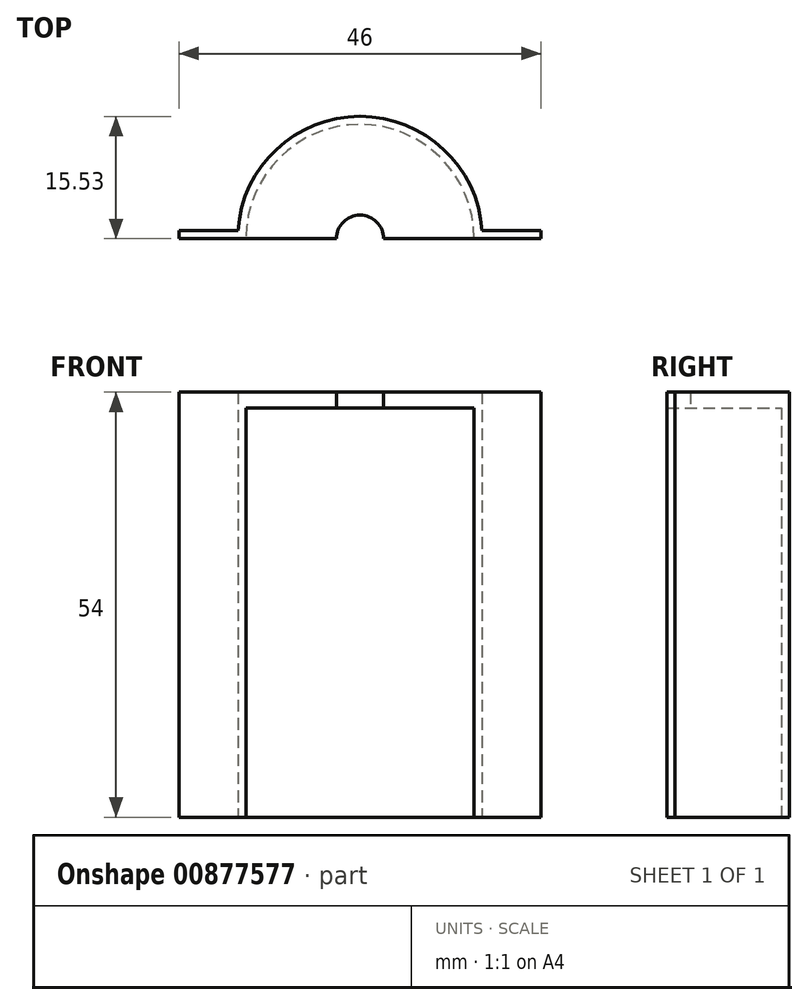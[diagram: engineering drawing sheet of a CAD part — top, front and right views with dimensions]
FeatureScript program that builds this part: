
annotation { "Feature Type Name" : "Feature", "Feature Type Description" : "" }
export const myFeature = defineFeature(function(context is Context, id is Id, definition is map)
    precondition{}
    {
        {
            var Q0;
            Q0=qCreatedBy(makeId("Top.planeOp"),FACE);
            var sketch = newSketch(context, id + "F0", { "sketchPlane" : qUnion([Q0])});
            skLineSegment(sketch, "E0", {"start": v(-21.63, 0) * mm, "end": v(-13.13, 0) * mm});
            skLineSegment(sketch, "E1", {"start": v(-21.63, 0) * mm, "end": v(-21.63, 1) * mm});
            skLineSegment(sketch, "E2", {"start": v(15.87, 0) * mm, "end": v(24.37, 0) * mm});
            skLineSegment(sketch, "E3", {"start": v(24.37, 0) * mm, "end": v(24.37, 1) * mm});
            skLineSegment(sketch, "E4", {"start": v(24.37, 1) * mm, "end": v(16.87, 1) * mm});
            skArc(sketch, "E5", {"start": v(15.87, 0) * mm, "mid": v(1.37, 14.5) * mm, "end": v(-13.13, 0) * mm});
            skLineSegment(sketch, "E6", {"start": v(-13.13, 0) * mm, "end": v(15.87, 0) * mm, "construction": true});
            skLineSegment(sketch, "E7", {"start": v(-21.63, 1) * mm, "end": v(-14.13, 1) * mm});
            skArc(sketch, "E8", {"start": v(16.87, 1) * mm, "mid": v(1.37, 15.53) * mm, "end": v(-14.13, 1) * mm});
            skSolve(sketch);
        }
        {
            var Q0;
            Q0=makeQuery(id+"F0.imprint","IMPRINT",FACE,{"disambiguationData":[TD([[makeQuery(id+"F0.imprint","IMPRINT",EDGE,{"derivedFrom":sQuery(id+"F0.wireOp",EDGE,"E0")}),1.0]])]});
            extrude(context, id + "F1", {"entities" : qUnion([Q0]), "endBound" : BoundingType.SYMMETRIC, "depth" : 52 * mm, "offsetDistance" : 25 * mm});
        }
        {
            var Q0;
            Q0=makeQuery(id+"F1.opExtrude","CAP_FACE",FACE,{"disambiguationData":[OSD([sQuery(id+"F0.wireOp",EDGE,"E0"),sQuery(id+"F0.wireOp",EDGE,"E1"),sQuery(id+"F0.wireOp",EDGE,"E2"),sQuery(id+"F0.wireOp",EDGE,"E3"),sQuery(id+"F0.wireOp",EDGE,"E4"),sQuery(id+"F0.wireOp",EDGE,"E5"),sQuery(id+"F0.wireOp",EDGE,"E7"),sQuery(id+"F0.wireOp",EDGE,"E8")])],"isStart":false});
            var sketch = newSketch(context, id + "F2", { "sketchPlane" : qUnion([Q0])});
            skLineSegment(sketch, "E9", {"start": v(-13.13, 0) * mm, "end": v(15.87, 0) * mm});
            skCircle(sketch, "E10", {"center": v(1.37, 0) * mm, "radius": 3 * mm});
            skSolve(sketch);
        }
        {
            var Q0;
            Q0=makeQuery(id+"F2.imprint","IMPRINT",FACE,{"disambiguationData":[TD([[makeQuery(id+"F2.imprint","IMPRINT",EDGE,{"derivedFrom":makeQuery(id+"F1.opExtrude","CAP_EDGE",EDGE,{"disambiguationData":[OSD([sQuery(id+"F0.wireOp",EDGE,"E0")])],"isStart":false})}),1.0]])]});
            var Q1;
            Q1=makeQuery(id+"F2.imprint","IMPRINT",FACE,{"disambiguationData":[TD([[makeQuery(id+"F2.imprint","IMPRINT",EDGE,{"derivedFrom":sQuery(id+"F2.wireOp",EDGE,"E9")}),1.0]])]});
            extrude(context, id + "F3", {"entities" : qUnion([Q0, Q1]), "operationType" : NewBodyOperationType.ADD, "depth" : 2 * mm, "offsetDistance" : 25 * mm});
        }
    });
